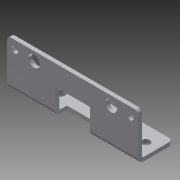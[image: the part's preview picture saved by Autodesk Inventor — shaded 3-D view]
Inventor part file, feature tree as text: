
AUTODESK INVENTOR PART (.ipt)
format: ipt  version: 2014 SP1 (Build 180222100, 222)  size: 264,704 bytes
history: native  units: in
note: dims shown in document units (in); Inventor stores cm internally (conversion verified against a paired STEP export)
features: other x7, sketch x6, sheet_metal_op x3, reference x3, chamfer x1, plane x1
ambient origin geometry x8: Origin, YZ Plane, XZ Plane, XY Plane, X Axis, Y Axis, Z Axis, Center Point
bodies: Solid1 (feature_tree)
feature tree (21):
  sheet_metal_op  "Face1"
  sheet_metal_op  "Flange1"
  chamfer  "Corner Round1"
  plane  "Work Plane1"
  sketch  "Sketch1"  dims[d0=4.25in]
  other  "Plate1"
  sketch  "Sketch2"  dims[d1=1.125in]
  other  "Plate2"
  sheet_metal_op  "Bend1"
  sketch  "Sketch3"  dims[d3=0.125in]
  sketch  "Sketch4"  dims[d4=0.125in]
  sketch  "Sketch5"  dims[d5=0.0625in]
  reference  "Reference1"
  sketch  "Sketch6"  dims[d6=0.25in d7=0.125in d8=1.5in d9=90.0deg d10=0.05in d11=0.5in d12=0.125in d13=0.125in d18=1.125in d20=0.375in d21=0.0in d22=0.625in d23=0.26in d24=0.26in d25=2.0in d26=1.0in d27=0.125in d28=0.0in d29=0.125in d30=0.125in d31=0.0in d32=0.125in d33=0.0in d34=0.375in d35=0.375in d36=0.875in d37=0.875in d38=0.25in d39=0.25in d2=0.125in]
  reference  "Reference11"
  reference  "Reference12"
  other  "Cut1"
  other  "Cut2"
  other  "Cut3"
  other  "Cut4"
  other  "Definition1"
